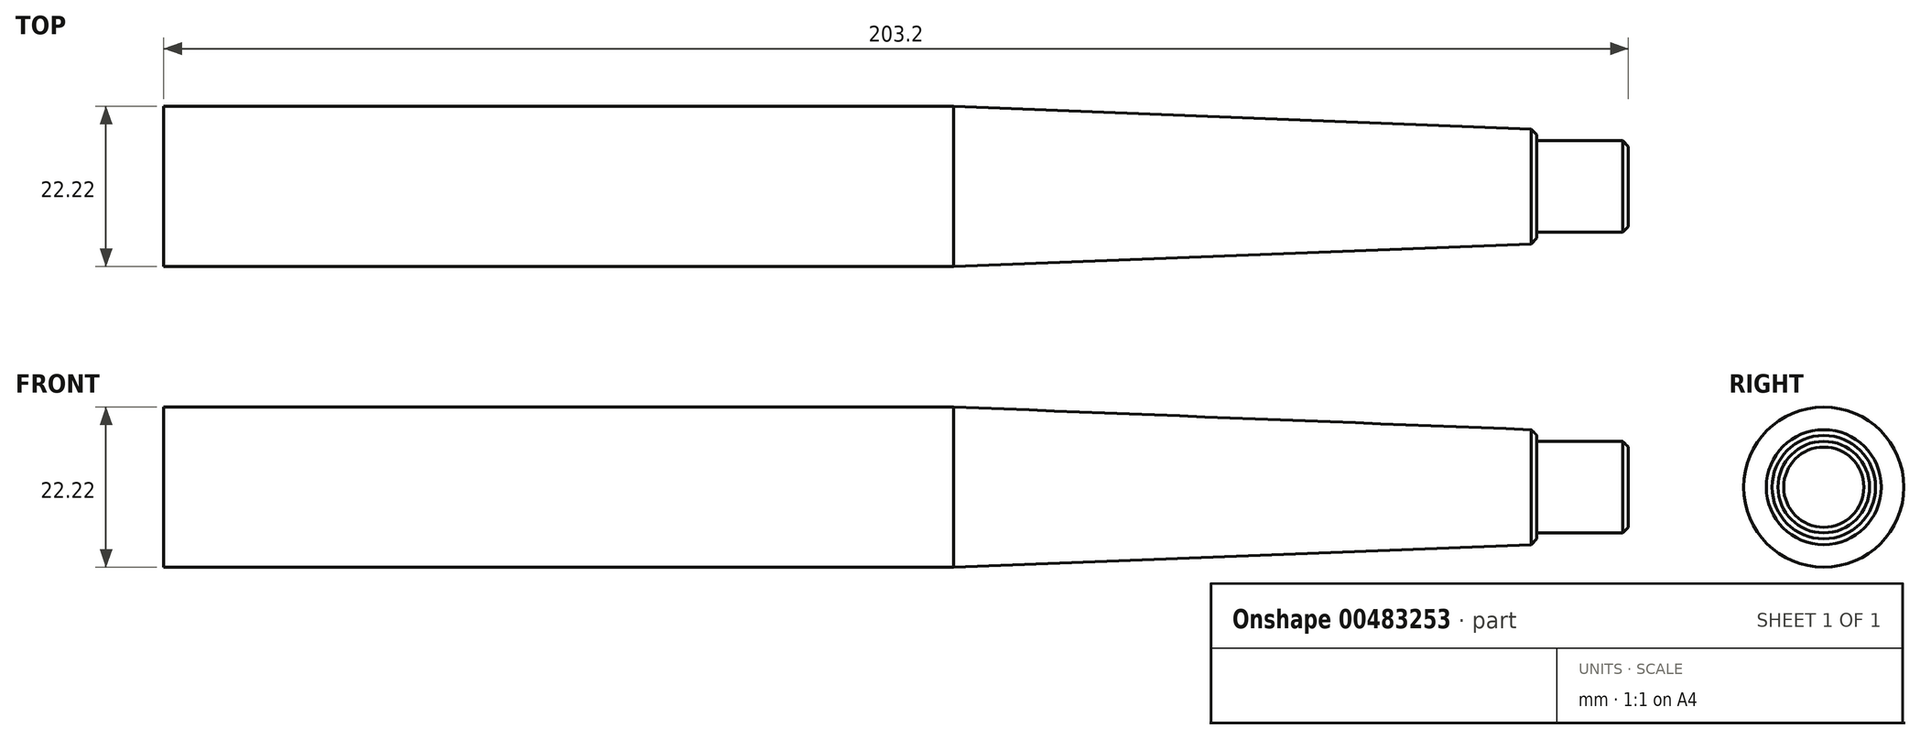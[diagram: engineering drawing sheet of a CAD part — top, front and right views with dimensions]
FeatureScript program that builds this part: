
annotation { "Feature Type Name" : "Feature", "Feature Type Description" : "" }
export const myFeature = defineFeature(function(context is Context, id is Id, definition is map)
    precondition{}
    {
        {
            var Q0;
            Q0=qCreatedBy(makeId("Front.planeOp"),FACE);
            var sketch = newSketch(context, id + "F0", { "sketchPlane" : qUnion([Q0])});
            skLineSegment(sketch, "E0", {"start": v(0, 0) * mm, "end": v(203.2, 0) * mm});
            skLineSegment(sketch, "E1", {"start": v(203.2, 0) * mm, "end": v(203.2, 6.35) * mm});
            skLineSegment(sketch, "E2", {"start": v(203.2, 6.35) * mm, "end": v(190.5, 6.35) * mm});
            skLineSegment(sketch, "E3", {"start": v(190.5, 6.35) * mm, "end": v(190.5, 7.94) * mm});
            skLineSegment(sketch, "E4", {"start": v(190.5, 7.94) * mm, "end": v(109.6, 11.11) * mm});
            skLineSegment(sketch, "E5", {"start": v(109.6, 11.11) * mm, "end": v(0, 11.11) * mm});
            skLineSegment(sketch, "E6", {"start": v(0, 11.11) * mm, "end": v(0, 0) * mm});
            skSolve(sketch);
        }
        {
            var Q0;
            Q0 = qSketchRegion(id + "F0", true);
            var Q1;
            Q1=sQuery(id+"F0.wireOp",EDGE,"E0");
            revolve(context, id + "F1", {"entities" : qUnion([Q0]), "axis" : qUnion([Q1]), "revolveType" : RevolveType.FULL});
        }
        {
            var Q0;
            Q0=makeQuery(id+"F1.opRevolve","SWEPT_EDGE",EDGE,{"disambiguationData":[OSD([sQuery(id+"F0.wireOp",EDGE,"E3"),sQuery(id+"F0.wireOp",EDGE,"E4")])]});
            chamfer(context, id + "F2", {"entities" : qUnion([Q0]), "width" : 0.8 * mm, "tangentPropagation" : true});
        }
        {
            var Q0;
            Q0=makeQuery(id+"F1.opRevolve","SWEPT_EDGE",EDGE,{"disambiguationData":[OSD([sQuery(id+"F0.wireOp",EDGE,"E1"),sQuery(id+"F0.wireOp",EDGE,"E2")])]});
            chamfer(context, id + "F3", {"entities" : qUnion([Q0]), "width" : 0.8 * mm, "tangentPropagation" : true});
        }
    });
